# Revit family: 303_R29X_
name_source: partatom
category: Pipe Accessories
revit_build: Autodesk Revit 2018 (Build: 20170223_1515(x64)
units: mm (PartAtom-declared; Revit-internal decimal feet)

## family parameters
Always vertical = Yes
Cut with Voids When Loaded = No
Part Type = Valve - Breaks Into
Round Connector Dimension = Use Diameter
Shared = No
Work Plane-Based = No

## types (5) — shared parameters
CAT0 = Yes
CAT1 = No
CenSd_W2_6 = 13 mm
Description = Angle lockshield valve for heat systems
L2D_Min = 3048 mm  [stored 10 ft]
M1 = 18 mm
M11 = 21 mm  [stored 0.0688976 ft]
M12 = 13 mm
M3 = 20 mm  [stored 0.0656168 ft]
M3__ve = -20 mm
Manufacturer = Giacomini
QmdConnectorList = 301;D;302;D1
URL = http://www.giacomini.com
W1 = 12 mm  [stored 0.0393701 ft]
W2 = 15 mm  [stored 0.0492126 ft]
W3 = 9 mm  [stored 0.0295276 ft]
X1 = 20 mm  [stored 0.0656168 ft]
Z1 = 2 mm  [stored 0.00656168 ft]
Z2 = 15 mm  [stored 0.0492126 ft]
magiPartTypeId = 303
magiProductFamilyId = R29X*
zero-valued in all types: MC_Default_elevation

## per-type parameters (varying)
| type | B1 | B4 | D | D1 | G3 | H3 | H3__ve | J1 | J3 | L | L2D | L3 | L4 | L4__ve | L5 | R1 | SW1 | SW2 | W2D | X11 | Z4 |
| R29X032 | 8 mm  [stored 0.0262467 ft] | 12 mm  [stored 0.0393701 ft] | 16 mm | 10 mm | 10 mm  [stored 0.0328084 ft] | 11 mm  [stored 0.0360892 ft] | -11 mm | 7 mm  [stored 0.0229659 ft] | 9 mm  [stored 0.0295276 ft] | 40 mm  [stored 0.131234 ft] | 40 mm  [stored 0.131234 ft] | 7 mm  [stored 0.0229659 ft] | 7 mm  [stored 0.0229659 ft] | -7 mm | 3 mm  [stored 0.00984252 ft] | 8 mm  [stored 0.0262467 ft] | Yes | No | 16 mm  [stored 0.0524934 ft] | 37 mm | 13 mm |
| R29X036 | 8 mm  [stored 0.0262467 ft] | 13 mm | 22 mm | 20 mm | 15 mm  [stored 0.0492126 ft] | 17 mm | -17 mm | 11 mm  [stored 0.0360892 ft] | 13 mm | 45 mm | 45 mm | 9 mm  [stored 0.0295276 ft] | 9 mm  [stored 0.0295276 ft] | -9 mm  [stored -0.0295276 ft] | 4 mm  [stored 0.0131234 ft] | 13 mm | No | Yes | 22 mm | 41 mm | 19 mm  [stored 0.062336 ft] |
| R29X035 | 7 mm  [stored 0.0229659 ft] | 11 mm  [stored 0.0360892 ft] | 18 mm | 20 mm | 15 mm  [stored 0.0492126 ft] | 12 mm  [stored 0.0393701 ft] | -12 mm  [stored -0.0393701 ft] | 7 mm  [stored 0.0229659 ft] | 9 mm  [stored 0.0295276 ft] | 45 mm | 45 mm | 9 mm  [stored 0.0295276 ft] | 9 mm  [stored 0.0295276 ft] | -9 mm  [stored -0.0295276 ft] | 4 mm  [stored 0.0131234 ft] | 13 mm | No | Yes | 18 mm | 41 mm | 14 mm  [stored 0.0459318 ft] |
| R29X034 | 7 mm  [stored 0.0229659 ft] | 11 mm  [stored 0.0360892 ft] | 18 mm | 15 mm | 12 mm  [stored 0.0393701 ft] | 12 mm  [stored 0.0393701 ft] | -12 mm  [stored -0.0393701 ft] | 7 mm  [stored 0.0229659 ft] | 9 mm  [stored 0.0295276 ft] | 41 mm | 41 mm | 7 mm  [stored 0.0229659 ft] | 7 mm  [stored 0.0229659 ft] | -7 mm | 4 mm  [stored 0.0131234 ft] | 11 mm  [stored 0.0360892 ft] | Yes | No | 18 mm | 38 mm | 14 mm  [stored 0.0459318 ft] |
| R29X033 | 8 mm  [stored 0.0262467 ft] | 12 mm  [stored 0.0393701 ft] | 16 mm | 15 mm | 12 mm  [stored 0.0393701 ft] | 11 mm  [stored 0.0360892 ft] | -11 mm | 7 mm  [stored 0.0229659 ft] | 9 mm  [stored 0.0295276 ft] | 40 mm  [stored 0.131234 ft] | 40 mm  [stored 0.131234 ft] | 7 mm  [stored 0.0229659 ft] | 7 mm  [stored 0.0229659 ft] | -7 mm | 3 mm  [stored 0.00984252 ft] | 11 mm  [stored 0.0360892 ft] | Yes | No | 16 mm  [stored 0.0524934 ft] | 37 mm | 13 mm |

note: column(s) folded — value = type name in every type: magiProductCode, magiProductId

note: [stored X ft] marks values corroborated as IEEE doubles in the binary element streams (Revit-internal decimal feet)

## geometry (parser evidence)
native form markers: Sweep x2
no freeform markers — native parametric forms only
